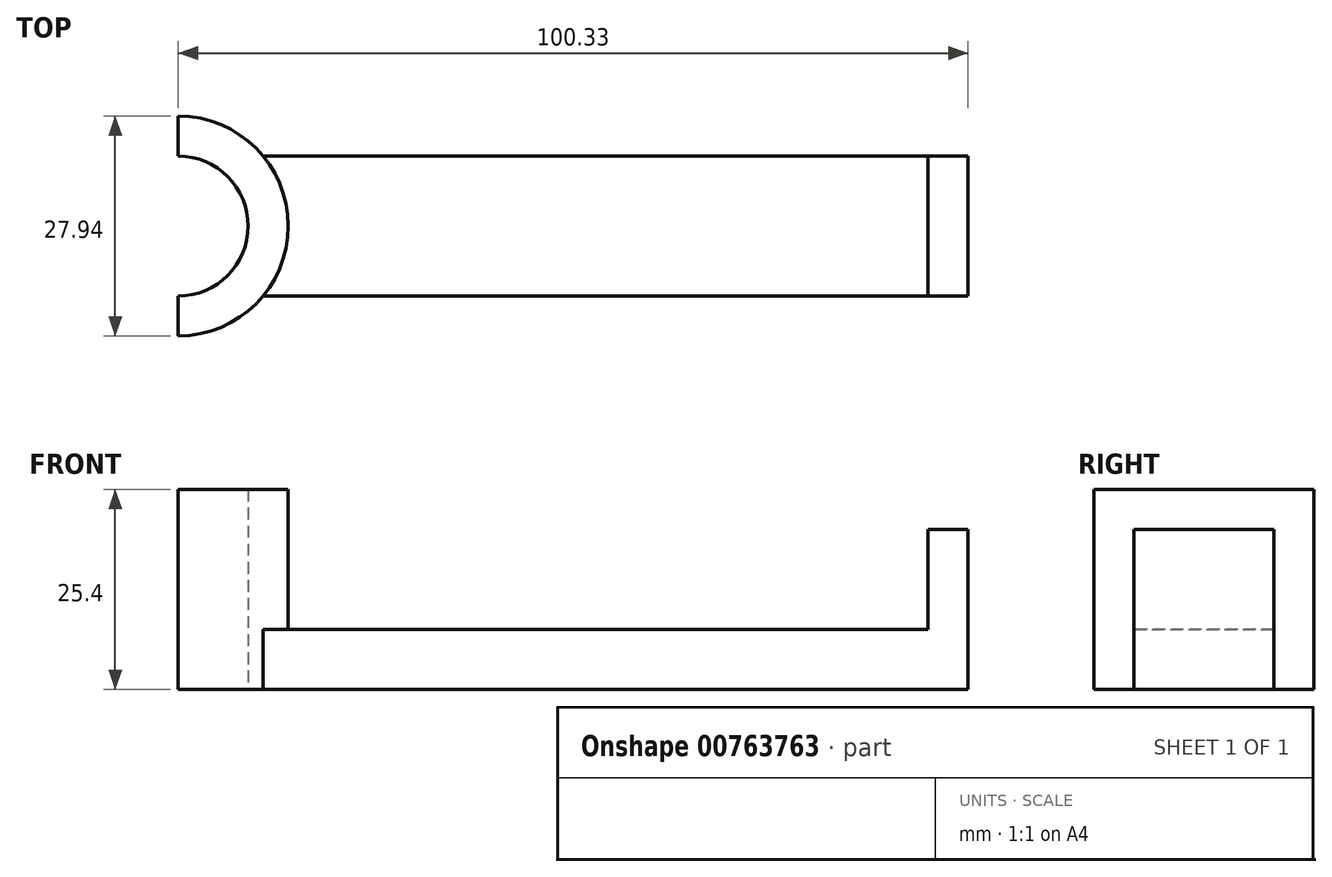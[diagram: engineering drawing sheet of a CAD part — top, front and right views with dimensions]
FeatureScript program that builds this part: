
annotation { "Feature Type Name" : "Feature", "Feature Type Description" : "" }
export const myFeature = defineFeature(function(context is Context, id is Id, definition is map)
    precondition{}
    {
        {
            var Q0;
            Q0=qCreatedBy(makeId("Top.planeOp"),FACE);
            var sketch = newSketch(context, id + "F0", { "sketchPlane" : qUnion([Q0])});
            skArc(sketch, "E0", {"start": v(0, -8.9) * mm, "mid": v(8.9, 0) * mm, "end": v(0, 8.9) * mm});
            skArc(sketch, "E1", {"start": v(0, -13.97) * mm, "mid": v(13.97, 0) * mm, "end": v(0, 13.97) * mm});
            skLineSegment(sketch, "E2", {"start": v(0, 13.97) * mm, "end": v(0, 8.89) * mm});
            skLineSegment(sketch, "E3.trimOffspring", {"start": v(0, -8.89) * mm, "end": v(0, -13.97) * mm});
            skSolve(sketch);
        }
        {
            var Q0;
            Q0=qSketchRegion(id+"F0",true);
            var Q1;
            Q1=makeQuery(id+"F0.imprint","IMPRINT",FACE,{"disambiguationData":[TD([[makeQuery(id+"F0.imprint","IMPRINT",EDGE,{"derivedFrom":sQuery(id+"F0.wireOp",EDGE,"E0")}),-1.0]])]});
            extrude(context, id + "F1", {"entities" : qUnion([Q0, Q1]), "depth" : 25.4 * mm, "offsetDistance" : 25.4 * mm});
        }
        {
            var Q0;
            Q0=makeQuery(id+"F1.opExtrude","CAP_FACE",FACE,{"disambiguationData":[OSD([sQuery(id+"F0.wireOp",EDGE,"E0"),sQuery(id+"F0.wireOp",EDGE,"E1"),sQuery(id+"F0.wireOp",EDGE,"E2"),sQuery(id+"F0.wireOp",EDGE,"E3.trimOffspring")])],"isStart":true});
            var sketch = newSketch(context, id + "F2", { "sketchPlane" : qUnion([Q0])});
            skLineSegment(sketch, "E4", {"start": v(0, 8.9) * mm, "end": v(100.33, 8.9) * mm});
            skLineSegment(sketch, "E5", {"start": v(100.33, 8.9) * mm, "end": v(100.33, -8.89) * mm});
            skLineSegment(sketch, "E6", {"start": v(100.33, -8.89) * mm, "end": v(0, -8.9) * mm});
            skSolve(sketch);
        }
        {
            var Q0;
            {var subQ1=sQuery(id+"F2.wireOp",EDGE,"E5");Q0=makeQuery(id+"F2.imprint","IMPRINT",FACE,{"disambiguationData":[TD([[makeQuery(id+"F2.imprint","IMPRINT",EDGE,{"derivedFrom":subQ1}),-1.0]])]});}
            extrude(context, id + "F3", {"entities" : qUnion([Q0]), "operationType" : NewBodyOperationType.ADD, "oppositeDirection" : true, "depth" : 7.62 * mm, "offsetDistance" : 25.4 * mm});
        }
        {
            var Q0;
            Q0=makeQuery(id+"F3.opExtrude","CAP_FACE",FACE,{"disambiguationData":[OSD([sQuery(id+"F0.wireOp",EDGE,"E1"),sQuery(id+"F2.wireOp",EDGE,"E4"),sQuery(id+"F2.wireOp",EDGE,"E5"),sQuery(id+"F2.wireOp",EDGE,"E6")])],"isStart":false});
            var sketch = newSketch(context, id + "F4", { "sketchPlane" : qUnion([Q0])});
            skLineSegment(sketch, "E7", {"start": v(95.25, 8.89) * mm, "end": v(95.25, -8.9) * mm});
            skSolve(sketch);
        }
        {
            var Q0;
            {var subQ0=sQuery(id+"F4.wireOp",EDGE,"E7");Q0=makeQuery(id+"F4.imprint","IMPRINT",FACE,{"disambiguationData":[TD([[makeQuery(id+"F4.imprint","IMPRINT",EDGE,{"derivedFrom":subQ0}),1.0]])]});}
            extrude(context, id + "F5", {"entities" : qUnion([Q0]), "operationType" : NewBodyOperationType.ADD, "depth" : 12.7 * mm, "offsetDistance" : 25.4 * mm});
        }
    });
